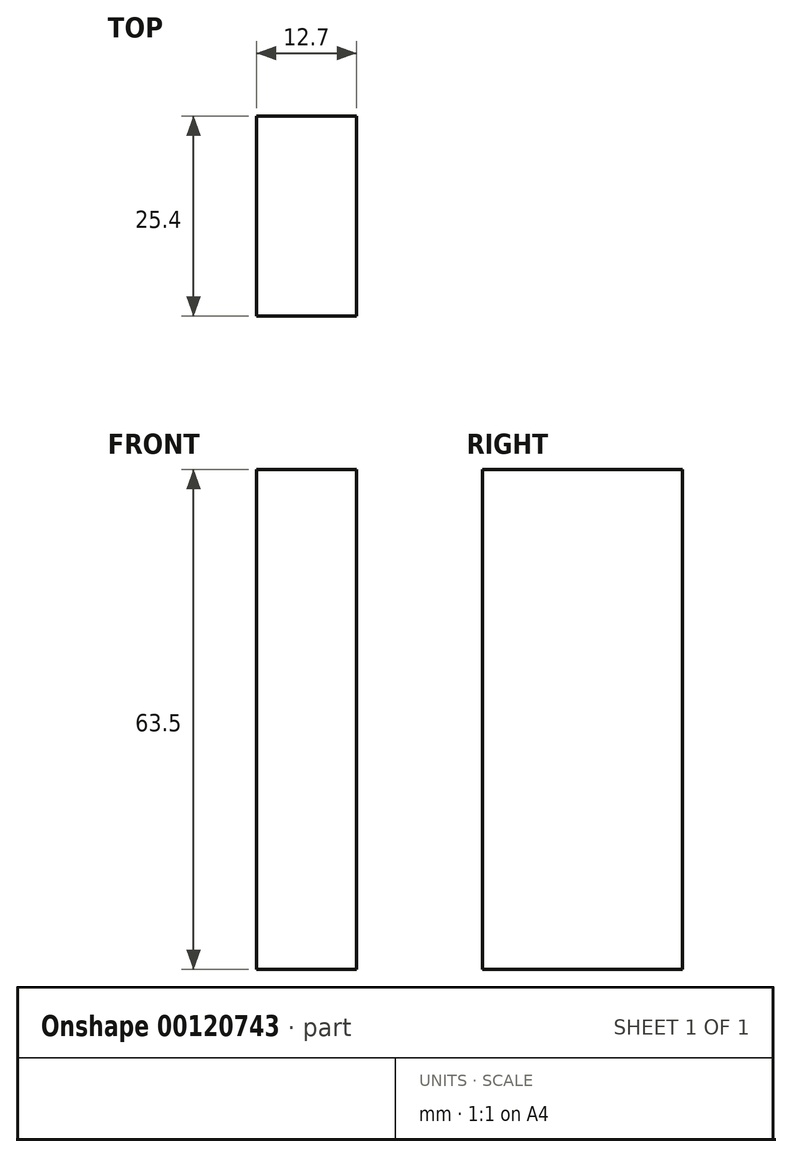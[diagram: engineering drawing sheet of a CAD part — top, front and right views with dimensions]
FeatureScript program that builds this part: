
annotation { "Feature Type Name" : "Feature", "Feature Type Description" : "" }
export const myFeature = defineFeature(function(context is Context, id is Id, definition is map)
    precondition{}
    {
        {
            var Q0;
            Q0=qCreatedBy(makeId("Front.planeOp"),FACE);
            var sketch = newSketch(context, id + "F0", { "sketchPlane" : qUnion([Q0])});
            skLineSegment(sketch, "E0.bottom", {"start": v(6.35, 31.75) * mm, "end": v(-6.35, 31.75) * mm});
            skLineSegment(sketch, "E0.top", {"start": v(6.35, -31.75) * mm, "end": v(-6.35, -31.75) * mm});
            skLineSegment(sketch, "E0.left", {"start": v(6.35, 31.75) * mm, "end": v(6.35, -31.75) * mm});
            skLineSegment(sketch, "E0.right", {"start": v(-6.35, 31.75) * mm, "end": v(-6.35, -31.75) * mm});
            skPoint(sketch, "E0.middle", {"position": v(0, 0) * mm});
            skSolve(sketch);
        }
        {
            var Q0;
            Q0 = qSketchRegion(id + "F0", true);
            extrude(context, id + "F1", {"entities" : qUnion([Q0]), "depth" : 25.4 * mm});
        }
    });
